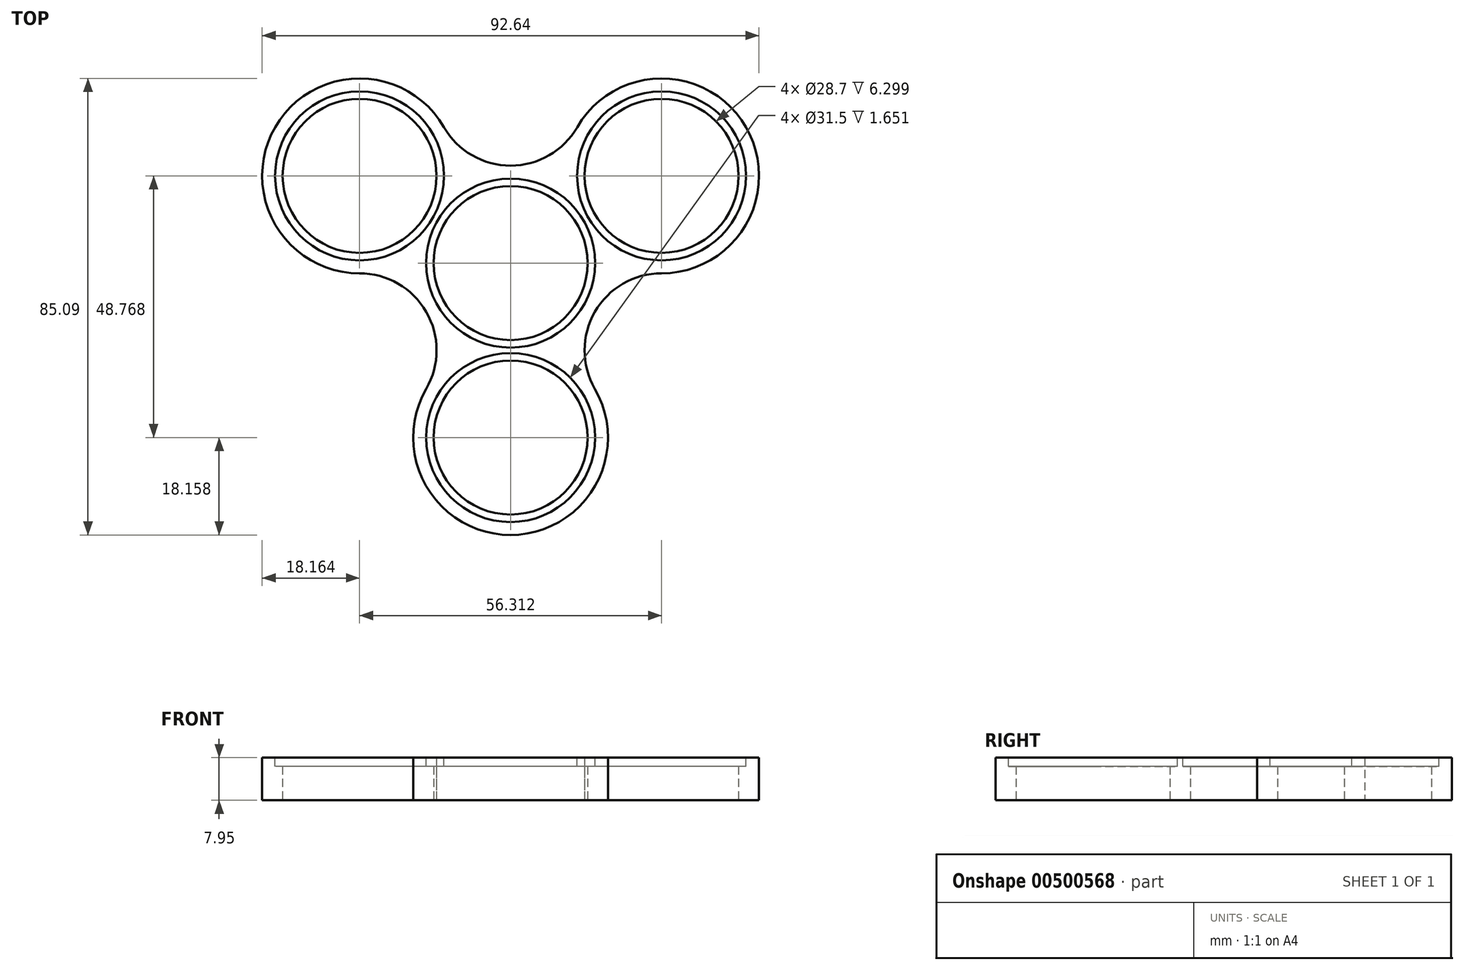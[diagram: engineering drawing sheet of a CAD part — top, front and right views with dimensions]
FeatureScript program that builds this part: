
annotation { "Feature Type Name" : "Feature", "Feature Type Description" : "" }
export const myFeature = defineFeature(function(context is Context, id is Id, definition is map)
    precondition{}
    {
        {
            var Q0;
            Q0=qCreatedBy(makeId("Top.planeOp"),FACE);
            var sketch = newSketch(context, id + "F0", { "sketchPlane" : qUnion([Q0])});
            skCircle(sketch, "E0", {"center": v(0, 0) * mm, "radius": 14.35 * mm});
            skCircle(sketch, "E1", {"center": v(-28.16, 16.26) * mm, "radius": 14.35 * mm});
            skArc(sketch, "E2.0", {"start": v(-12.43, 25.34) * mm, "mid": v(-43.88, 25.34) * mm, "end": v(-28.16, -1.9) * mm});
            skCircle(sketch, "E3", {"center": v(28.16, 16.26) * mm, "radius": 14.35 * mm});
            skArc(sketch, "E4.0", {"start": v(28.16, -1.9) * mm, "mid": v(43.88, 25.34) * mm, "end": v(12.43, 25.34) * mm});
            skCircle(sketch, "E5", {"center": v(0, -32.51) * mm, "radius": 14.35 * mm});
            skArc(sketch, "E6.0", {"start": v(-15.73, -23.43) * mm, "mid": v(0, -50.67) * mm, "end": v(15.73, -23.43) * mm});
            skArc(sketch, "E7", {"start": v(28.16, -1.9) * mm, "mid": v(15.73, -9.08) * mm, "end": v(15.73, -23.43) * mm});
            skLineSegment(sketch, "E8", {"start": v(-0.04, -0.47) * mm, "end": v(0, 0) * mm});
            skArc(sketch, "E9", {"start": v(-12.43, 25.34) * mm, "mid": v(0, 18.16) * mm, "end": v(12.43, 25.34) * mm});
            skArc(sketch, "E10", {"start": v(-15.73, -23.43) * mm, "mid": v(-15.73, -9.08) * mm, "end": v(-28.16, -1.9) * mm});
            skSolve(sketch);
        }
        {
            var Q0;
            Q0=makeQuery(id+"F0.imprint","IMPRINT",FACE,{"disambiguationData":[TD([[makeQuery(id+"F0.imprint","IMPRINT",EDGE,{"derivedFrom":sQuery(id+"F0.wireOp",EDGE,"E0")}),-1.0]])]});
            extrude(context, id + "F1", {"entities" : qUnion([Q0]), "depth" : 7.95 * mm, "offsetDistance" : 25.4 * mm});
        }
        {
            var Q0;
            Q0=makeQuery(id+"F1.opExtrude","CAP_FACE",FACE,{"disambiguationData":[OSD([sQuery(id+"F0.wireOp",EDGE,"E0"),sQuery(id+"F0.wireOp",EDGE,"E1"),sQuery(id+"F0.wireOp",EDGE,"E2.0"),sQuery(id+"F0.wireOp",EDGE,"E3"),sQuery(id+"F0.wireOp",EDGE,"E4.0"),sQuery(id+"F0.wireOp",EDGE,"E5"),sQuery(id+"F0.wireOp",EDGE,"E6.0"),sQuery(id+"F0.wireOp",EDGE,"E7"),sQuery(id+"F0.wireOp",EDGE,"E9"),sQuery(id+"F0.wireOp",EDGE,"E10")])],"isStart":false});
            var sketch = newSketch(context, id + "F2", { "sketchPlane" : qUnion([Q0])});
            skCircle(sketch, "E11.0", {"center": v(-28.16, 16.26) * mm, "radius": 15.75 * mm});
            skCircle(sketch, "E12.0", {"center": v(28.16, 16.26) * mm, "radius": 15.75 * mm});
            skCircle(sketch, "E13.0", {"center": v(0, -32.51) * mm, "radius": 15.75 * mm});
            skCircle(sketch, "E14.0", {"center": v(0, 0) * mm, "radius": 15.75 * mm});
            skSolve(sketch);
        }
        {
            var Q0;
            Q0=makeQuery(id+"F2.imprint","IMPRINT",FACE,{"disambiguationData":[TD([[makeQuery(id+"F2.imprint","IMPRINT",EDGE,{"derivedFrom":sQuery(id+"F2.wireOp",EDGE,"E11.0")}),1.0]])]});
            var Q1;
            Q1=sQuery(id+"F2.wireOp",EDGE,"E13.0");
            extrude(context, id + "F3", {"entities" : qUnion([Q0]), "operationType" : NewBodyOperationType.REMOVE, "surfaceEntities" : qUnion([Q1]), "oppositeDirection" : true, "depth" : 1.65 * mm, "offsetDistance" : 25.4 * mm});
        }
        {
            var Q0;
            Q0=makeQuery(id+"F2.imprint","IMPRINT",FACE,{"disambiguationData":[TD([[makeQuery(id+"F2.imprint","IMPRINT",EDGE,{"derivedFrom":sQuery(id+"F2.wireOp",EDGE,"E12.0")}),1.0]])]});
            extrude(context, id + "F4", {"entities" : qUnion([Q0]), "operationType" : NewBodyOperationType.REMOVE, "oppositeDirection" : true, "depth" : 1.65 * mm, "offsetDistance" : 25.4 * mm});
        }
        {
            var Q0;
            Q0=makeQuery(id+"F2.imprint","IMPRINT",FACE,{"disambiguationData":[TD([[makeQuery(id+"F2.imprint","IMPRINT",EDGE,{"derivedFrom":sQuery(id+"F2.wireOp",EDGE,"E13.0")}),1.0]])]});
            var Q1;
            Q1=sQuery(id+"F2.wireOp",EDGE,"E13.0");
            extrude(context, id + "F5", {"entities" : qUnion([Q0]), "operationType" : NewBodyOperationType.REMOVE, "surfaceEntities" : qUnion([Q1]), "oppositeDirection" : true, "depth" : 1.65 * mm, "offsetDistance" : 25.4 * mm});
        }
        {
            var Q0;
            Q0=makeQuery(id+"F2.imprint","IMPRINT",FACE,{"disambiguationData":[TD([[makeQuery(id+"F2.imprint","IMPRINT",EDGE,{"derivedFrom":sQuery(id+"F2.wireOp",EDGE,"E14.0")}),1.0]])]});
            extrude(context, id + "F6", {"entities" : qUnion([Q0]), "operationType" : NewBodyOperationType.REMOVE, "oppositeDirection" : true, "depth" : 1.65 * mm, "offsetDistance" : 25.4 * mm});
        }
    });
